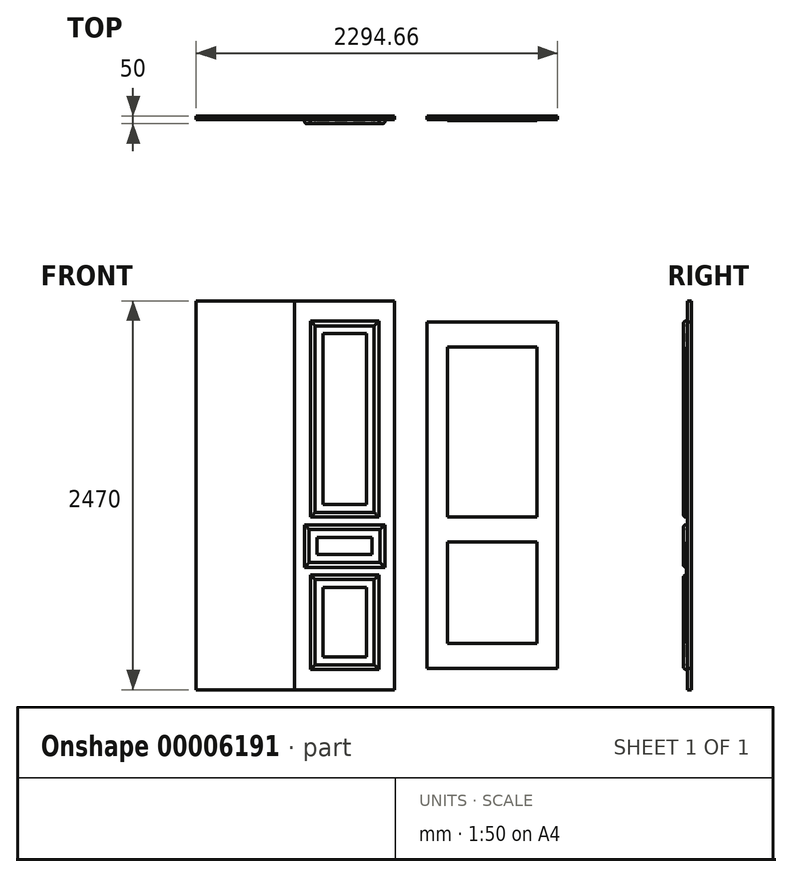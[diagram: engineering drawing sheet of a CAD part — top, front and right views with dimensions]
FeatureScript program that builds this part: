
annotation { "Feature Type Name" : "Feature", "Feature Type Description" : "" }
export const myFeature = defineFeature(function(context is Context, id is Id, definition is map)
    precondition{}
    {
        {
            var Q0;
            Q0=qCreatedBy(makeId("Front.planeOp"),FACE);
            var sketch = newSketch(context, id + "F0", { "sketchPlane" : qUnion([Q0])});
            skLineSegment(sketch, "E0.rect.bottom", {"start": v(630, -1235) * mm, "end": v(-630, -1235) * mm});
            skLineSegment(sketch, "E0.rect.top", {"start": v(630, 1235) * mm, "end": v(-630, 1235) * mm});
            skLineSegment(sketch, "E0.rect.left", {"start": v(630, -1235) * mm, "end": v(630, 1235) * mm});
            skLineSegment(sketch, "E0.rect.right", {"start": v(-630, -1235) * mm, "end": v(-630, 1235) * mm});
            skPoint(sketch, "E0.rect.middle", {"position": v(0, 0) * mm});
            skLineSegment(sketch, "E1", {"start": v(-5, 1235) * mm, "end": v(-5, -1235) * mm});
            skSolve(sketch);
        }
        {
            var Q0;
            {var subQ1=sQuery(id+"F0.wireOp",EDGE,"E0.rect.left");Q0=makeQuery(id+"F0.imprint","IMPRINT",FACE,{"disambiguationData":[TD([[makeQuery(id+"F0.imprint","IMPRINT",EDGE,{"derivedFrom":subQ1}),1.0]])]});}
            var Q1;
            {var subQ1=sQuery(id+"F0.wireOp",EDGE,"E0.rect.right");Q1=makeQuery(id+"F0.imprint","IMPRINT",FACE,{"disambiguationData":[TD([[makeQuery(id+"F0.imprint","IMPRINT",EDGE,{"derivedFrom":subQ1}),-1.0]])]});}
            extrude(context, id + "F1", {"entities" : qUnion([Q0, Q1]), "depth" : 25 * mm});
        }
        {
            var Q0;
            Q0=makeQuery(id+"F1.opExtrude","CAP_FACE",FACE,{"disambiguationData":[OSD([sQuery(id+"F0.wireOp",EDGE,"E0.rect.bottom"),sQuery(id+"F0.wireOp",EDGE,"E0.rect.top"),sQuery(id+"F0.wireOp",EDGE,"E0.rect.left"),sQuery(id+"F0.wireOp",EDGE,"E0.rect.right")])],"isStart":false});
            var sketch = newSketch(context, id + "F2", { "sketchPlane" : qUnion([Q0])});
            skLineSegment(sketch, "E2", {"start": v(-5, 1235) * mm, "end": v(-5, -1235) * mm, "construction": true});
            skLineSegment(sketch, "E3.rect.bottom", {"start": v(-5.5, -1235) * mm, "end": v(-4.5, -1235) * mm});
            skLineSegment(sketch, "E3.rect.top", {"start": v(-5.5, 1235) * mm, "end": v(-4.5, 1235) * mm});
            skLineSegment(sketch, "E3.rect.left", {"start": v(-5.5, -1235) * mm, "end": v(-5.5, 1235) * mm});
            skLineSegment(sketch, "E3.rect.right", {"start": v(-4.5, -1235) * mm, "end": v(-4.5, 1235) * mm});
            skPoint(sketch, "E3.rect.middle", {"position": v(-5, 0) * mm});
            skSolve(sketch);
        }
        {
            var Q0;
            Q0=makeQuery(id+"F2.imprint","IMPRINT",FACE,{"disambiguationData":[TD([[makeQuery(id+"F2.imprint","IMPRINT",EDGE,{"derivedFrom":sQuery(id+"F2.wireOp",EDGE,"E3.rect.bottom")}),-1.0]])]});
            extrude(context, id + "F3", {"entities" : qUnion([Q0]), "operationType" : NewBodyOperationType.REMOVE, "oppositeDirection" : true, "depth" : 25 * mm});
        }
        {
            var Q0;
            {var subQ0=sQuery(id+"F0.wireOp",EDGE,"E0.rect.bottom");var subQ1=sQuery(id+"F0.wireOp",EDGE,"E0.rect.top");var subQ2=sQuery(id+"F0.wireOp",EDGE,"E0.rect.left");Q0=makeQuery(id+"F3.boolean.opBoolean","SPLIT",FACE,{"disambiguationData":[TD([makeQuery(id+"F1.opExtrude","SWEPT_FACE",FACE,{"disambiguationData":[OSD([subQ2])]})])],"derivedFrom":makeQuery(id+"F1.opExtrude","CAP_FACE",FACE,{"disambiguationData":[OSD([subQ0,subQ1,subQ2,sQuery(id+"F0.wireOp",EDGE,"E0.rect.right")])],"isStart":false})});}
            var sketch = newSketch(context, id + "F4", { "sketchPlane" : qUnion([Q0])});
            skLineSegment(sketch, "E4", {"start": v(312.75, 1235) * mm, "end": v(312.75, -1235) * mm, "construction": true});
            skLineSegment(sketch, "E5.rect.bottom", {"start": v(450.25, -58.75) * mm, "end": v(175.25, -58.75) * mm});
            skLineSegment(sketch, "E5.rect.top", {"start": v(450.25, 1026.25) * mm, "end": v(175.25, 1026.25) * mm});
            skLineSegment(sketch, "E5.rect.left", {"start": v(450.25, -58.75) * mm, "end": v(450.25, 1026.25) * mm});
            skLineSegment(sketch, "E5.rect.right", {"start": v(175.25, -58.75) * mm, "end": v(175.25, 1026.25) * mm});
            skPoint(sketch, "E5.rect.middle", {"position": v(312.75, 483.75) * mm});
            skLineSegment(sketch, "E6.rect.bottom", {"start": v(137.75, -267.5) * mm, "end": v(487.75, -267.5) * mm});
            skLineSegment(sketch, "E6.rect.top", {"start": v(137.75, -377.5) * mm, "end": v(487.75, -377.5) * mm});
            skLineSegment(sketch, "E6.rect.left", {"start": v(137.75, -267.5) * mm, "end": v(137.75, -377.5) * mm});
            skLineSegment(sketch, "E6.rect.right", {"start": v(487.75, -267.5) * mm, "end": v(487.75, -377.5) * mm});
            skPoint(sketch, "E6.rect.middle", {"position": v(312.75, -322.5) * mm});
            skLineSegment(sketch, "E7.rect.bottom", {"start": v(450.25, -1026.25) * mm, "end": v(175.25, -1026.25) * mm});
            skLineSegment(sketch, "E7.rect.top", {"start": v(450.25, -586.25) * mm, "end": v(175.25, -586.25) * mm});
            skLineSegment(sketch, "E7.rect.left", {"start": v(450.25, -1026.25) * mm, "end": v(450.25, -586.25) * mm});
            skLineSegment(sketch, "E7.rect.right", {"start": v(175.25, -1026.25) * mm, "end": v(175.25, -586.25) * mm});
            skPoint(sketch, "E7.rect.middle", {"position": v(312.75, -806.25) * mm});
            skLineSegment(sketch, "E8.0", {"start": v(125.25, -108.75) * mm, "end": v(125.25, 1076.25) * mm});
            skLineSegment(sketch, "E8.1", {"start": v(500.25, -108.75) * mm, "end": v(125.25, -108.75) * mm});
            skLineSegment(sketch, "E8.2", {"start": v(500.25, -108.75) * mm, "end": v(500.25, 1076.25) * mm});
            skLineSegment(sketch, "E8.3", {"start": v(500.25, 1076.25) * mm, "end": v(125.25, 1076.25) * mm});
            skLineSegment(sketch, "E9.0", {"start": v(95.25, -138.75) * mm, "end": v(95.25, 1106.25) * mm});
            skLineSegment(sketch, "E9.1", {"start": v(530.25, -138.75) * mm, "end": v(95.25, -138.75) * mm});
            skLineSegment(sketch, "E9.2", {"start": v(530.25, -138.75) * mm, "end": v(530.25, 1106.25) * mm});
            skLineSegment(sketch, "E9.3", {"start": v(530.25, 1106.25) * mm, "end": v(95.25, 1106.25) * mm});
            skLineSegment(sketch, "E10.0", {"start": v(87.75, -217.5) * mm, "end": v(537.75, -217.5) * mm});
            skLineSegment(sketch, "E10.1", {"start": v(87.75, -217.5) * mm, "end": v(87.75, -427.5) * mm});
            skLineSegment(sketch, "E10.2", {"start": v(87.75, -427.5) * mm, "end": v(537.75, -427.5) * mm});
            skLineSegment(sketch, "E10.3", {"start": v(537.75, -217.5) * mm, "end": v(537.75, -427.5) * mm});
            skLineSegment(sketch, "E11.0", {"start": v(57.75, -187.5) * mm, "end": v(57.75, -457.5) * mm});
            skLineSegment(sketch, "E11.1", {"start": v(57.75, -187.5) * mm, "end": v(567.75, -187.5) * mm});
            skLineSegment(sketch, "E11.2", {"start": v(567.75, -187.5) * mm, "end": v(567.75, -457.5) * mm});
            skLineSegment(sketch, "E11.3", {"start": v(57.75, -457.5) * mm, "end": v(567.75, -457.5) * mm});
            skLineSegment(sketch, "E12.0", {"start": v(500.25, -536.25) * mm, "end": v(125.25, -536.25) * mm});
            skLineSegment(sketch, "E12.1", {"start": v(500.25, -1076.25) * mm, "end": v(500.25, -536.25) * mm});
            skLineSegment(sketch, "E12.2", {"start": v(500.25, -1076.25) * mm, "end": v(125.25, -1076.25) * mm});
            skLineSegment(sketch, "E12.3", {"start": v(125.25, -1076.25) * mm, "end": v(125.25, -536.25) * mm});
            skLineSegment(sketch, "E13.0", {"start": v(530.25, -506.25) * mm, "end": v(95.25, -506.25) * mm});
            skLineSegment(sketch, "E13.1", {"start": v(530.25, -1106.25) * mm, "end": v(530.25, -506.25) * mm});
            skLineSegment(sketch, "E13.2", {"start": v(530.25, -1106.25) * mm, "end": v(95.25, -1106.25) * mm});
            skLineSegment(sketch, "E13.3", {"start": v(95.25, -1106.25) * mm, "end": v(95.25, -506.25) * mm});
            skSolve(sketch);
        }
        {
            var Q0;
            Q0=makeQuery(id+"F4.imprint","IMPRINT",FACE,{"disambiguationData":[TD([[makeQuery(id+"F4.imprint","IMPRINT",EDGE,{"derivedFrom":sQuery(id+"F4.wireOp",EDGE,"E5.rect.bottom")}),-1.0]])]});
            var Q1;
            Q1=makeQuery(id+"F4.imprint","IMPRINT",FACE,{"disambiguationData":[TD([[makeQuery(id+"F4.imprint","IMPRINT",EDGE,{"derivedFrom":sQuery(id+"F4.wireOp",EDGE,"E6.rect.bottom")}),-1.0]])]});
            var Q2;
            Q2=makeQuery(id+"F4.imprint","IMPRINT",FACE,{"disambiguationData":[TD([[makeQuery(id+"F4.imprint","IMPRINT",EDGE,{"derivedFrom":sQuery(id+"F4.wireOp",EDGE,"E7.rect.bottom")}),-1.0]])]});
            var Q3;
            Q3=makeQuery(id+"F4.imprint","IMPRINT",FACE,{"disambiguationData":[TD([[makeQuery(id+"F4.imprint","IMPRINT",EDGE,{"derivedFrom":sQuery(id+"F4.wireOp",EDGE,"E8.0")}),1.0]])]});
            var Q4;
            Q4=makeQuery(id+"F4.imprint","IMPRINT",FACE,{"disambiguationData":[TD([[makeQuery(id+"F4.imprint","IMPRINT",EDGE,{"derivedFrom":sQuery(id+"F4.wireOp",EDGE,"E10.0")}),1.0]])]});
            var Q5;
            Q5=makeQuery(id+"F4.imprint","IMPRINT",FACE,{"disambiguationData":[TD([[makeQuery(id+"F4.imprint","IMPRINT",EDGE,{"derivedFrom":sQuery(id+"F4.wireOp",EDGE,"E12.0")}),-1.0]])]});
            extrude(context, id + "F5", {"entities" : qUnion([Q0, Q1, Q2, Q3, Q4, Q5]), "operationType" : NewBodyOperationType.ADD, "depth" : 25 * mm});
        }
        {
            var Q0;
            Q0=makeQuery(id+"F5.opExtrude","CAP_EDGE",EDGE,{"disambiguationData":[OSD([sQuery(id+"F4.wireOp",EDGE,"E9.3")])],"isStart":false});
            var Q1;
            Q1=makeQuery(id+"F5.opExtrude","CAP_EDGE",EDGE,{"disambiguationData":[OSD([sQuery(id+"F4.wireOp",EDGE,"E8.3")])],"isStart":false});
            var Q2;
            Q2=makeQuery(id+"F5.opExtrude","CAP_EDGE",EDGE,{"disambiguationData":[OSD([sQuery(id+"F4.wireOp",EDGE,"E9.2")])],"isStart":false});
            var Q3;
            Q3=makeQuery(id+"F5.opExtrude","CAP_EDGE",EDGE,{"disambiguationData":[OSD([sQuery(id+"F4.wireOp",EDGE,"E8.2")])],"isStart":false});
            var Q4;
            Q4=makeQuery(id+"F5.opExtrude","CAP_EDGE",EDGE,{"disambiguationData":[OSD([sQuery(id+"F4.wireOp",EDGE,"E8.0")])],"isStart":false});
            var Q5;
            Q5=makeQuery(id+"F5.opExtrude","CAP_EDGE",EDGE,{"disambiguationData":[OSD([sQuery(id+"F4.wireOp",EDGE,"E9.0")])],"isStart":false});
            var Q6;
            Q6=makeQuery(id+"F5.opExtrude","CAP_EDGE",EDGE,{"disambiguationData":[OSD([sQuery(id+"F4.wireOp",EDGE,"E8.1")])],"isStart":false});
            var Q7;
            Q7=makeQuery(id+"F5.opExtrude","CAP_EDGE",EDGE,{"disambiguationData":[OSD([sQuery(id+"F4.wireOp",EDGE,"E9.1")])],"isStart":false});
            var Q8;
            Q8=makeQuery(id+"F5.opExtrude","CAP_EDGE",EDGE,{"disambiguationData":[OSD([sQuery(id+"F4.wireOp",EDGE,"E11.1")])],"isStart":false});
            var Q9;
            Q9=makeQuery(id+"F5.opExtrude","CAP_EDGE",EDGE,{"disambiguationData":[OSD([sQuery(id+"F4.wireOp",EDGE,"E10.0")])],"isStart":false});
            var Q10;
            Q10=makeQuery(id+"F5.opExtrude","CAP_EDGE",EDGE,{"disambiguationData":[OSD([sQuery(id+"F4.wireOp",EDGE,"E11.2")])],"isStart":false});
            var Q11;
            Q11=makeQuery(id+"F5.opExtrude","CAP_EDGE",EDGE,{"disambiguationData":[OSD([sQuery(id+"F4.wireOp",EDGE,"E10.3")])],"isStart":false});
            var Q12;
            Q12=makeQuery(id+"F5.opExtrude","CAP_EDGE",EDGE,{"disambiguationData":[OSD([sQuery(id+"F4.wireOp",EDGE,"E10.1")])],"isStart":false});
            var Q13;
            Q13=makeQuery(id+"F5.opExtrude","CAP_EDGE",EDGE,{"disambiguationData":[OSD([sQuery(id+"F4.wireOp",EDGE,"E11.0")])],"isStart":false});
            var Q14;
            Q14=makeQuery(id+"F5.opExtrude","CAP_EDGE",EDGE,{"disambiguationData":[OSD([sQuery(id+"F4.wireOp",EDGE,"E10.2")])],"isStart":false});
            var Q15;
            Q15=makeQuery(id+"F5.opExtrude","CAP_EDGE",EDGE,{"disambiguationData":[OSD([sQuery(id+"F4.wireOp",EDGE,"E11.3")])],"isStart":false});
            var Q16;
            Q16=makeQuery(id+"F5.opExtrude","CAP_EDGE",EDGE,{"disambiguationData":[OSD([sQuery(id+"F4.wireOp",EDGE,"E13.0")])],"isStart":false});
            var Q17;
            Q17=makeQuery(id+"F5.opExtrude","CAP_EDGE",EDGE,{"disambiguationData":[OSD([sQuery(id+"F4.wireOp",EDGE,"E12.0")])],"isStart":false});
            var Q18;
            Q18=makeQuery(id+"F5.opExtrude","CAP_EDGE",EDGE,{"disambiguationData":[OSD([sQuery(id+"F4.wireOp",EDGE,"E13.1")])],"isStart":false});
            var Q19;
            Q19=makeQuery(id+"F5.opExtrude","CAP_EDGE",EDGE,{"disambiguationData":[OSD([sQuery(id+"F4.wireOp",EDGE,"E12.1")])],"isStart":false});
            var Q20;
            Q20=makeQuery(id+"F5.opExtrude","CAP_EDGE",EDGE,{"disambiguationData":[OSD([sQuery(id+"F4.wireOp",EDGE,"E12.3")])],"isStart":false});
            var Q21;
            Q21=makeQuery(id+"F5.opExtrude","CAP_EDGE",EDGE,{"disambiguationData":[OSD([sQuery(id+"F4.wireOp",EDGE,"E13.3")])],"isStart":false});
            var Q22;
            Q22=makeQuery(id+"F5.opExtrude","CAP_EDGE",EDGE,{"disambiguationData":[OSD([sQuery(id+"F4.wireOp",EDGE,"E12.2")])],"isStart":false});
            var Q23;
            Q23=makeQuery(id+"F5.opExtrude","CAP_EDGE",EDGE,{"disambiguationData":[OSD([sQuery(id+"F4.wireOp",EDGE,"E13.2")])],"isStart":false});
            fillet(context, id + "F6", {"entities" : qUnion([Q0, Q1, Q2, Q3, Q4, Q5, Q6, Q7, Q8, Q9, Q10, Q11, Q12, Q13, Q14, Q15, Q16, Q17, Q18, Q19, Q20, Q21, Q22, Q23]), "radius" : 15 * mm, "tangentPropagation" : true, "allowEdgeOverflow" : false});
        }
        {
            var Q0;
            Q0=makeQuery(id+"F5.opExtrude","CAP_FACE",FACE,{"disambiguationData":[OSD([sQuery(id+"F4.wireOp",EDGE,"E5.rect.bottom"),sQuery(id+"F4.wireOp",EDGE,"E5.rect.top"),sQuery(id+"F4.wireOp",EDGE,"E5.rect.left"),sQuery(id+"F4.wireOp",EDGE,"E5.rect.right")])],"isStart":false});
            var Q1;
            Q1=makeQuery(id+"F5.opExtrude","CAP_FACE",FACE,{"disambiguationData":[OSD([sQuery(id+"F4.wireOp",EDGE,"E6.rect.bottom"),sQuery(id+"F4.wireOp",EDGE,"E6.rect.top"),sQuery(id+"F4.wireOp",EDGE,"E6.rect.left"),sQuery(id+"F4.wireOp",EDGE,"E6.rect.right")])],"isStart":false});
            var Q2;
            Q2=makeQuery(id+"F5.opExtrude","CAP_FACE",FACE,{"disambiguationData":[OSD([sQuery(id+"F4.wireOp",EDGE,"E7.rect.bottom"),sQuery(id+"F4.wireOp",EDGE,"E7.rect.top"),sQuery(id+"F4.wireOp",EDGE,"E7.rect.left"),sQuery(id+"F4.wireOp",EDGE,"E7.rect.right")])],"isStart":false});
            extrude(context, id + "F7", {"entities" : qUnion([Q0, Q1, Q2]), "operationType" : NewBodyOperationType.REMOVE, "oppositeDirection" : true, "depth" : 20 * mm});
        }
        {
            var Q0;
            Q0=qCreatedBy(makeId("Front.planeOp"),FACE);
            var sketch = newSketch(context, id + "F8", { "sketchPlane" : qUnion([Q0])});
            skLineSegment(sketch, "E14.rect.bottom", {"start": v(1664.66, -1100) * mm, "end": v(834.66, -1100) * mm});
            skLineSegment(sketch, "E14.rect.top", {"start": v(1664.66, 1100) * mm, "end": v(834.66, 1100) * mm});
            skLineSegment(sketch, "E14.rect.left", {"start": v(1664.66, -1100) * mm, "end": v(1664.66, 1100) * mm});
            skLineSegment(sketch, "E14.rect.right", {"start": v(834.66, -1100) * mm, "end": v(834.66, 1100) * mm});
            skPoint(sketch, "E14.rect.middle", {"position": v(1249.66, 0) * mm});
            skSolve(sketch);
        }
        {
            var Q0;
            Q0=makeQuery(id+"F8.imprint","IMPRINT",FACE,{"disambiguationData":[TD([[makeQuery(id+"F8.imprint","IMPRINT",EDGE,{"derivedFrom":sQuery(id+"F8.wireOp",EDGE,"E14.rect.bottom")}),-1.0]])]});
            extrude(context, id + "F9", {"entities" : qUnion([Q0]), "depth" : 25 * mm});
        }
        {
            var Q0;
            Q0=makeQuery(id+"F9.opExtrude","CAP_FACE",FACE,{"disambiguationData":[OSD([sQuery(id+"F8.wireOp",EDGE,"E14.rect.bottom"),sQuery(id+"F8.wireOp",EDGE,"E14.rect.top"),sQuery(id+"F8.wireOp",EDGE,"E14.rect.left"),sQuery(id+"F8.wireOp",EDGE,"E14.rect.right")])],"isStart":false});
            var sketch = newSketch(context, id + "F10", { "sketchPlane" : qUnion([Q0])});
            skLineSegment(sketch, "E15", {"start": v(1249.66, 1100) * mm, "end": v(1249.66, -1100) * mm, "construction": true});
            skLineSegment(sketch, "E16.rect.bottom", {"start": v(964.66, -138.33) * mm, "end": v(1534.66, -138.33) * mm});
            skLineSegment(sketch, "E16.rect.top", {"start": v(964.66, 941.67) * mm, "end": v(1534.66, 941.67) * mm});
            skLineSegment(sketch, "E16.rect.left", {"start": v(964.66, -138.33) * mm, "end": v(964.66, 941.67) * mm});
            skLineSegment(sketch, "E16.rect.right", {"start": v(1534.66, -138.33) * mm, "end": v(1534.66, 941.67) * mm});
            skPoint(sketch, "E16.rect.middle", {"position": v(1249.66, 401.67) * mm});
            skLineSegment(sketch, "E17.rect.bottom", {"start": v(1534.66, -941.67) * mm, "end": v(964.66, -941.67) * mm});
            skLineSegment(sketch, "E17.rect.top", {"start": v(1534.66, -296.67) * mm, "end": v(964.66, -296.67) * mm});
            skLineSegment(sketch, "E17.rect.left", {"start": v(1534.66, -941.67) * mm, "end": v(1534.66, -296.67) * mm});
            skLineSegment(sketch, "E17.rect.right", {"start": v(964.66, -941.67) * mm, "end": v(964.66, -296.67) * mm});
            skPoint(sketch, "E17.rect.middle", {"position": v(1249.66, -619.17) * mm});
            skSolve(sketch);
        }
        {
            var Q0;
            Q0=makeQuery(id+"F10.imprint","IMPRINT",FACE,{"disambiguationData":[TD([[makeQuery(id+"F10.imprint","IMPRINT",EDGE,{"derivedFrom":sQuery(id+"F10.wireOp",EDGE,"E16.rect.bottom")}),1.0]])]});
            var Q1;
            Q1=makeQuery(id+"F10.imprint","IMPRINT",FACE,{"disambiguationData":[TD([[makeQuery(id+"F10.imprint","IMPRINT",EDGE,{"derivedFrom":sQuery(id+"F10.wireOp",EDGE,"E17.rect.bottom")}),-1.0]])]});
            extrude(context, id + "F11", {"entities" : qUnion([Q0, Q1]), "operationType" : NewBodyOperationType.ADD, "depth" : 5 * mm});
        }
    });
